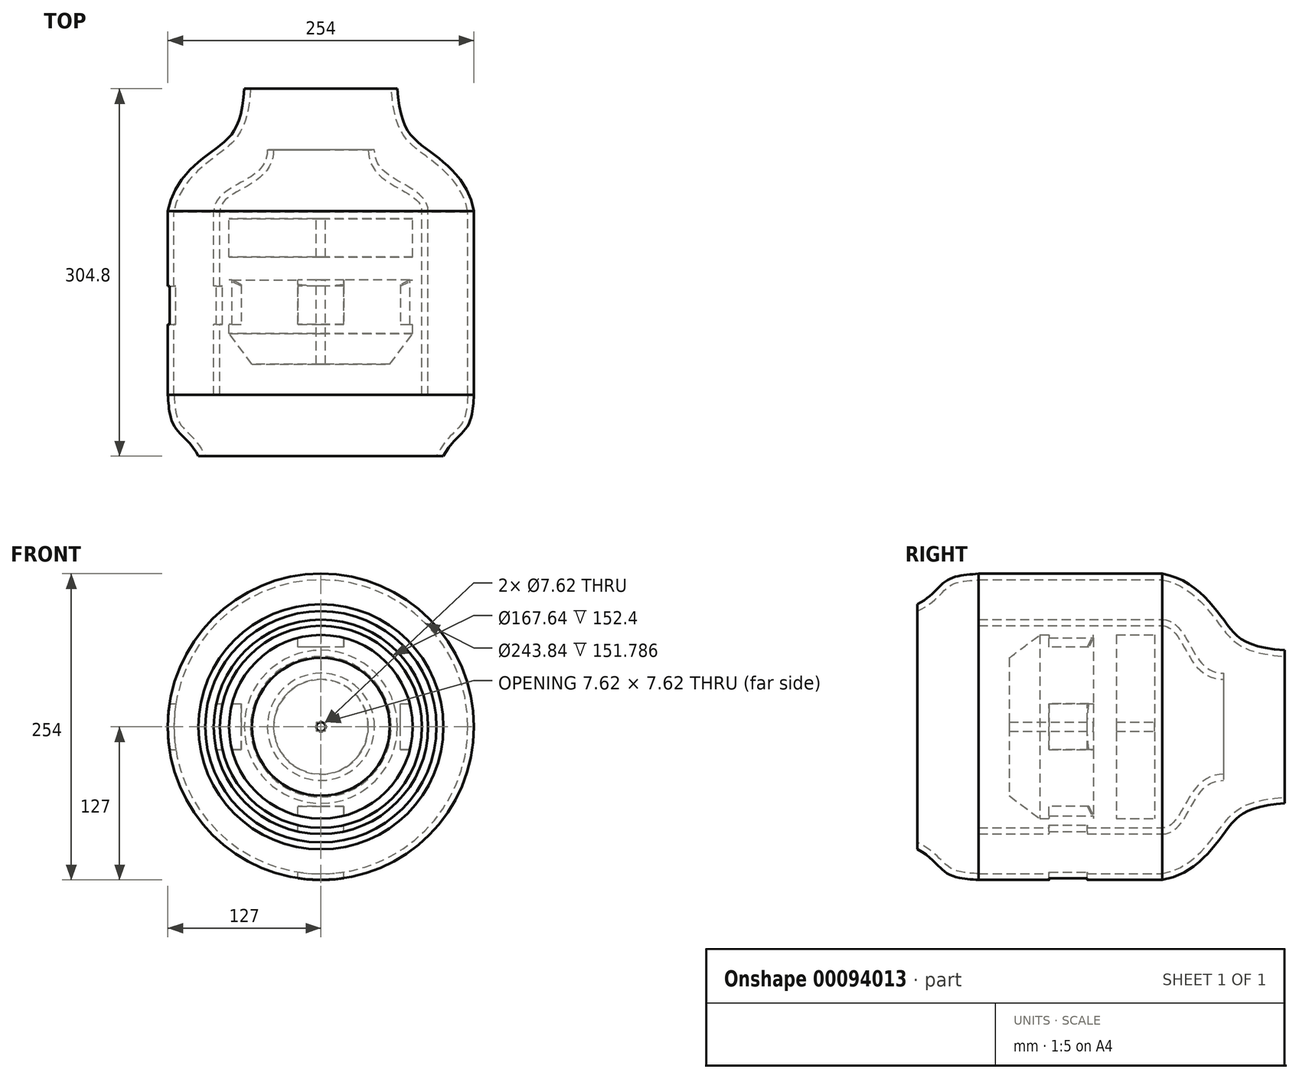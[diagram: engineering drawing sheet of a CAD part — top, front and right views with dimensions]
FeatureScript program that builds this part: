
annotation { "Feature Type Name" : "Feature", "Feature Type Description" : "" }
export const myFeature = defineFeature(function(context is Context, id is Id, definition is map)
    precondition{}
    {
        {
            var Q0;
            Q0=qCreatedBy(makeId("Right.planeOp"),FACE);
            var sketch = newSketch(context, id + "F0", { "sketchPlane" : qUnion([Q0])});
            skLineSegment(sketch, "E0", {"start": v(152.4, 0) * mm, "end": v(-152.4, 0) * mm});
            skPoint(sketch, "E1", {"position": v(0, 0) * mm});
            skLineSegment(sketch, "E2", {"start": v(-152.4, 0) * mm, "end": v(-152.4, 101.6) * mm});
            skLineSegment(sketch, "E3", {"start": v(-152.4, 101.6) * mm, "end": v(-127, 101.6) * mm, "construction": true});
            skLineSegment(sketch, "E4", {"start": v(-127, 101.6) * mm, "end": v(-127, 121.92) * mm, "construction": true});
            skLineSegment(sketch, "E5", {"start": v(-127, 101.6) * mm, "end": v(-101.6, 101.6) * mm, "construction": true});
            skLineSegment(sketch, "E6", {"start": v(-101.6, 101.6) * mm, "end": v(-101.6, 127) * mm, "construction": true});
            skFitSpline(sketch, "E7", {"points": [v(-152.4, 101.6) * mm, v(-127, 121.92) * mm, v(-101.6, 127) * mm], "startDerivative": vector(70.98, 35.75) * mm, "endDerivative": vector(55.23, 4.25) * mm});
            skLineSegment(sketch, "E8", {"start": v(-101.6, 127) * mm, "end": v(50.8, 127) * mm});
            skPoint(sketch, "E9", {"position": v(101.6, 0) * mm});
            skLineSegment(sketch, "E10", {"start": v(101.6, 0) * mm, "end": v(101.6, 88.9) * mm, "construction": true});
            skLineSegment(sketch, "E11", {"start": v(152.4, 0) * mm, "end": v(152.4, 63.5) * mm});
            skFitSpline(sketch, "E12", {"points": [v(50.8, 127) * mm, v(101.6, 88.9) * mm, v(152.4, 63.5) * mm], "startDerivative": vector(144.88, -23.56) * mm, "endDerivative": vector(213.2, -14.75) * mm});
            skLineSegment(sketch, "E13", {"start": v(-101.6, 127) * mm, "end": v(-101.6, 0) * mm, "construction": true});
            skLineSegment(sketch, "E14", {"start": v(-101.6, 0) * mm, "end": v(-101.6, 88.9) * mm});
            skLineSegment(sketch, "E15", {"start": v(-101.6, 88.9) * mm, "end": v(50.8, 88.9) * mm});
            skPoint(sketch, "E16", {"position": v(76.2, 0) * mm});
            skLineSegment(sketch, "E17", {"start": v(101.6, 0) * mm, "end": v(101.6, 44.45) * mm, "construction": true});
            skLineSegment(sketch, "E18", {"start": v(76.2, 0) * mm, "end": v(76.2, 63.5) * mm, "construction": true});
            skFitSpline(sketch, "E19", {"points": [v(50.8, 88.9) * mm, v(76.2, 63.5) * mm, v(101.6, 44.45) * mm], "startDerivative": vector(73.92, 0) * mm, "endDerivative": vector(78.63, 0) * mm});
            skLineSegment(sketch, "E20", {"start": v(101.6, 44.45) * mm, "end": v(76.2, 44.45) * mm, "construction": true});
            skLineSegment(sketch, "E21", {"start": v(50.8, 88.9) * mm, "end": v(76.2, 88.9) * mm, "construction": true});
            skLineSegment(sketch, "E22", {"start": v(101.6, 44.45) * mm, "end": v(101.6, 0) * mm});
            skPoint(sketch, "E23", {"position": v(-76.2, 0) * mm});
            skLineSegment(sketch, "E24", {"start": v(-76.2, 0) * mm, "end": v(-76.2, 57.15) * mm});
            skPoint(sketch, "E25", {"position": v(-50.8, 0) * mm});
            skLineSegment(sketch, "E26", {"start": v(-50.8, 0) * mm, "end": v(-50.8, 76.2) * mm, "construction": true});
            skLineSegment(sketch, "E27", {"start": v(-76.2, 57.15) * mm, "end": v(-50.8, 76.2) * mm});
            skLineSegment(sketch, "E28", {"start": v(-50.8, 76.2) * mm, "end": v(-6.35, 76.2) * mm});
            skLineSegment(sketch, "E29", {"start": v(-6.35, 76.2) * mm, "end": v(-6.35, 0) * mm});
            skLineSegment(sketch, "E30", {"start": v(-6.35, 0) * mm, "end": v(-76.2, 0) * mm});
            skPoint(sketch, "E31", {"position": v(12.7, 0) * mm});
            skLineSegment(sketch, "E32", {"start": v(12.7, 0) * mm, "end": v(12.7, 76.2) * mm});
            skLineSegment(sketch, "E33", {"start": v(12.7, 76.2) * mm, "end": v(44.45, 76.2) * mm});
            skLineSegment(sketch, "E34.bottom", {"start": v(-93.42, 127) * mm, "end": v(-7.63, 127) * mm});
            skLineSegment(sketch, "E35", {"start": v(44.45, 76.2) * mm, "end": v(44.45, 0) * mm});
            skSolve(sketch);
        }
        {
            var Q0;
            {var subQ4=sQuery(id+"F0.wireOp",EDGE,"E2");Q0=makeQuery(id+"F0.imprint","IMPRINT",FACE,{"disambiguationData":[TD([[makeQuery(id+"F0.imprint","IMPRINT",EDGE,{"derivedFrom":subQ4}),-1.0]])]});}
            var Q1;
            {var subQ0=sQuery(id+"F0.wireOp",EDGE,"E14");Q1=makeQuery(id+"F0.imprint","IMPRINT",FACE,{"disambiguationData":[TD([[makeQuery(id+"F0.imprint","IMPRINT",EDGE,{"derivedFrom":subQ0}),-1.0]])]});}
            var Q2;
            {var subQ0=sQuery(id+"F0.wireOp",EDGE,"E32");Q2=makeQuery(id+"F0.imprint","IMPRINT",FACE,{"disambiguationData":[TD([[makeQuery(id+"F0.imprint","IMPRINT",EDGE,{"derivedFrom":subQ0}),-1.0]])]});}
            var Q3;
            Q3=makeQuery(id+"F0.imprint","IMPRINT",FACE,{"disambiguationData":[TD([[makeQuery(id+"F0.imprint","IMPRINT",EDGE,{"derivedFrom":sQuery(id+"F0.wireOp",EDGE,"E24")}),-1.0]])]});
            var Q4;
            Q4=sQuery(id+"F0.wireOp",EDGE,"E0");
            revolve(context, id + "F1", {"entities" : qUnion([Q0, Q1, Q2, Q3]), "axis" : qUnion([Q4]), "revolveType" : RevolveType.FULL});
        }
        {
            var Q0;
            Q0=makeQuery(id+"F1.opRevolve","SWEPT_FACE",FACE,{"disambiguationData":[OSD([sQuery(id+"F0.wireOp",EDGE,"E2")])]});
            var Q1;
            Q1=makeQuery(id+"F1.opRevolve","SWEPT_FACE",FACE,{"disambiguationData":[OSD([sQuery(id+"F0.wireOp",EDGE,"E11")])]});
            shell(context, id + "F2", {"entities" : qUnion([Q0, Q1]), "thickness" : 5.08 * mm});
        }
        {
            var Q0;
            Q0=qCreatedBy(makeId("Front.planeOp"),FACE);
            var sketch = newSketch(context, id + "F3", { "sketchPlane" : qUnion([Q0])});
            skCircle(sketch, "E36", {"center": v(0, 0) * mm, "radius": 3.18 * mm});
            skCircle(sketch, "E37", {"center": v(0, 0) * mm, "radius": 3.81 * mm});
            skSolve(sketch);
        }
        {
            var Q0;
            {var subQ0=sQuery(id+"F0.wireOp",EDGE,"E14");Q0=makeQuery(id+"F0.imprint","IMPRINT",FACE,{"disambiguationData":[TD([[makeQuery(id+"F0.imprint","IMPRINT",EDGE,{"derivedFrom":subQ0}),-1.0]])]});}
            var Q1;
            Q1=makeQuery(id+"F0.imprint","IMPRINT",FACE,{"disambiguationData":[TD([[makeQuery(id+"F0.imprint","IMPRINT",EDGE,{"derivedFrom":sQuery(id+"F0.wireOp",EDGE,"E24")}),-1.0]])]});
            var Q2;
            {var subQ0=sQuery(id+"F0.wireOp",EDGE,"E32");Q2=makeQuery(id+"F0.imprint","IMPRINT",FACE,{"disambiguationData":[TD([[makeQuery(id+"F0.imprint","IMPRINT",EDGE,{"derivedFrom":subQ0}),-1.0]])]});}
            var Q3;
            Q3=sQuery(id+"F0.wireOp",EDGE,"E0");
            revolve(context, id + "F4", {"entities" : qUnion([Q0, Q1, Q2]), "axis" : qUnion([Q3]), "revolveType" : RevolveType.FULL});
        }
        {
            var Q0;
            Q0=makeQuery(id+"F4.opRevolve","SWEPT_FACE",FACE,{"disambiguationData":[OSD([sQuery(id+"F0.wireOp",EDGE,"E14")])]});
            var Q1;
            Q1=makeQuery(id+"F4.opRevolve","SWEPT_FACE",FACE,{"disambiguationData":[OSD([sQuery(id+"F0.wireOp",EDGE,"E22")])]});
            shell(context, id + "F5", {"entities" : qUnion([Q0, Q1]), "thickness" : 5.08 * mm});
        }
        {
            var Q0;
            Q0=makeQuery(id+"F0.imprint","IMPRINT",FACE,{"disambiguationData":[TD([[makeQuery(id+"F0.imprint","IMPRINT",EDGE,{"derivedFrom":sQuery(id+"F0.wireOp",EDGE,"E24")}),-1.0]])]});
            var Q1;
            {var subQ0=sQuery(id+"F0.wireOp",EDGE,"E32");Q1=makeQuery(id+"F0.imprint","IMPRINT",FACE,{"disambiguationData":[TD([[makeQuery(id+"F0.imprint","IMPRINT",EDGE,{"derivedFrom":subQ0}),-1.0]])]});}
            var Q2;
            Q2=sQuery(id+"F0.wireOp",EDGE,"E0");
            revolve(context, id + "F6", {"entities" : qUnion([Q0, Q1]), "axis" : qUnion([Q2]), "revolveType" : RevolveType.FULL});
        }
        {
            var Q0;
            Q0=makeQuery(id+"F3.imprint","IMPRINT",FACE,{"disambiguationData":[TD([[makeQuery(id+"F3.imprint","IMPRINT",EDGE,{"derivedFrom":sQuery(id+"F3.wireOp",EDGE,"E36")}),-1.0]])]});
            var Q1;
            Q1=makeQuery(id+"F3.imprint","IMPRINT",FACE,{"disambiguationData":[TD([[makeQuery(id+"F3.imprint","IMPRINT",EDGE,{"derivedFrom":sQuery(id+"F3.wireOp",EDGE,"E36")}),1.0]])]});
            extrude(context, id + "F7", {"entities" : qUnion([Q0, Q1]), "operationType" : NewBodyOperationType.REMOVE, "endBound" : BoundingType.SYMMETRIC, "depth" : 2540 * mm});
        }
        {
            var Q0;
            Q0=qCreatedBy(makeId("Top.planeOp"),FACE);
            cPlane(context, id + "F8", {"entities" : qUnion([Q0]), "cplaneType" : CPlaneType.OFFSET, "offset" : 76.2 * mm, "width" : 152.4 * mm, "height" : 152.4 * mm});
        }
        {
            var Q0;
            Q0=qCreatedBy(id+"F8.planeOp",FACE);
            var sketch = newSketch(context, id + "F9", { "sketchPlane" : qUnion([Q0])});
            skPoint(sketch, "E38", {"position": v(0, -6.35) * mm});
            skLineSegment(sketch, "E39", {"start": v(0, -6.35) * mm, "end": v(19.05, -6.35) * mm, "construction": true});
            skLineSegment(sketch, "E40", {"start": v(19.05, -6.35) * mm, "end": v(19.05, -11.43) * mm, "construction": true});
            skLineSegment(sketch, "E41.bottom", {"start": v(19.05, -11.43) * mm, "end": v(-19.05, -11.43) * mm});
            skLineSegment(sketch, "E41.top", {"start": v(19.05, -43.18) * mm, "end": v(-19.05, -43.18) * mm});
            skLineSegment(sketch, "E41.left", {"start": v(19.05, -11.43) * mm, "end": v(19.05, -43.18) * mm});
            skLineSegment(sketch, "E41.right", {"start": v(-19.05, -11.43) * mm, "end": v(-19.05, -43.18) * mm});
            skSolve(sketch);
        }
        {
            var Q0;
            Q0=makeQuery(id+"F9.imprint","IMPRINT",FACE,{"disambiguationData":[TD([[makeQuery(id+"F9.imprint","IMPRINT",EDGE,{"derivedFrom":sQuery(id+"F9.wireOp",EDGE,"E41.bottom")}),1.0]])]});
            extrude(context, id + "F10", {"entities" : qUnion([Q0]), "operationType" : NewBodyOperationType.REMOVE, "oppositeDirection" : true, "depth" : 10.16 * mm});
        }
        {
            var Q0;
            Q0 = qSketchRegion(id + "F9", true);
            extrude(context, id + "F11", {"entities" : qUnion([Q0]), "operationType" : NewBodyOperationType.REMOVE, "endBound" : BoundingType.THROUGH_ALL, "oppositeDirection" : true, "depth" : 25.4 * mm, "hasSecondDirection" : true, "secondDirectionOppositeDirection" : true, "secondDirectionDepth" : 142.24 * mm});
        }
        {
            var Q0;
            Q0=qCreatedBy(makeId("Right.planeOp"),FACE);
            cPlane(context, id + "F12", {"entities" : qUnion([Q0]), "cplaneType" : CPlaneType.OFFSET, "offset" : 76.2 * mm, "width" : 152.4 * mm, "height" : 152.4 * mm});
        }
        {
            var Q0;
            Q0=qCreatedBy(id+"F12.planeOp",FACE);
            var sketch = newSketch(context, id + "F13", { "sketchPlane" : qUnion([Q0])});
            skPoint(sketch, "E42", {"position": v(-6.35, 0) * mm});
            skLineSegment(sketch, "E43", {"start": v(-6.35, 0) * mm, "end": v(-11.43, 0) * mm, "construction": true});
            skLineSegment(sketch, "E44", {"start": v(-11.43, 0) * mm, "end": v(-27.3, 0) * mm, "construction": true});
            skLineSegment(sketch, "E45.bottom", {"start": v(-11.43, -19.05) * mm, "end": v(-43.18, -19.05) * mm});
            skLineSegment(sketch, "E45.top", {"start": v(-11.43, 19.05) * mm, "end": v(-43.18, 19.05) * mm});
            skLineSegment(sketch, "E45.left", {"start": v(-11.43, -19.05) * mm, "end": v(-11.43, 19.05) * mm});
            skLineSegment(sketch, "E45.right", {"start": v(-43.18, -19.05) * mm, "end": v(-43.18, 19.05) * mm});
            skPoint(sketch, "E45.middle", {"position": v(-27.3, 0) * mm});
            skSolve(sketch);
        }
        {
            var Q0;
            Q0=makeQuery(id+"F13.imprint","IMPRINT",FACE,{"disambiguationData":[TD([[makeQuery(id+"F13.imprint","IMPRINT",EDGE,{"derivedFrom":sQuery(id+"F13.wireOp",EDGE,"E45.bottom")}),-1.0]])]});
            extrude(context, id + "F14", {"entities" : qUnion([Q0]), "operationType" : NewBodyOperationType.REMOVE, "oppositeDirection" : true, "depth" : 10.16 * mm});
        }
        {
            var Q0;
            Q0 = qSketchRegion(id + "F13", true);
            var Q1;
            Q1 = qConstructionFilter(qBodyType(qCreatedBy(id + "F13" ,EDGE), BodyType.WIRE), ConstructionObject.NO);
            extrude(context, id + "F15", {"entities" : qUnion([Q0]), "operationType" : NewBodyOperationType.REMOVE, "surfaceEntities" : qUnion([Q1]), "endBound" : BoundingType.THROUGH_ALL, "oppositeDirection" : true, "depth" : 25.4 * mm, "hasSecondDirection" : true, "secondDirectionOppositeDirection" : true, "secondDirectionDepth" : 142.24 * mm});
        }
        {
            var Q0;
            Q0=makeQuery(id+"F10.boolean.opBoolean","INTERSECT",EDGE,{"derivedFrom":[makeQuery(id+"F6.opRevolve","SWEPT_FACE",FACE,{"disambiguationData":[OSD([sQuery(id+"F0.wireOp",EDGE,"E28")])]}),makeQuery(id+"F10.opExtrude","SWEPT_FACE",FACE,{"disambiguationData":[OSD([sQuery(id+"F9.wireOp",EDGE,"E41.bottom")])]})]});
            var Q1;
            Q1=makeQuery(id+"F11.boolean.opBoolean","INTERSECT",EDGE,{"derivedFrom":[makeQuery(id+"F6.opRevolve","SWEPT_FACE",FACE,{"disambiguationData":[OSD([sQuery(id+"F0.wireOp",EDGE,"E28")])]}),makeQuery(id+"F11.opExtrude","SWEPT_FACE",FACE,{"disambiguationData":[OSD([sQuery(id+"F9.wireOp",EDGE,"E41.bottom")])]})]});
            var Q2;
            Q2=makeQuery(id+"F15.boolean.opBoolean","INTERSECT",EDGE,{"derivedFrom":[makeQuery(id+"F6.opRevolve","SWEPT_FACE",FACE,{"disambiguationData":[OSD([sQuery(id+"F0.wireOp",EDGE,"E28")])]}),makeQuery(id+"F15.opExtrude","SWEPT_FACE",FACE,{"disambiguationData":[OSD([sQuery(id+"F13.wireOp",EDGE,"E45.left")])]})]});
            var Q3;
            Q3=makeQuery(id+"F14.boolean.opBoolean","INTERSECT",EDGE,{"derivedFrom":[makeQuery(id+"F6.opRevolve","SWEPT_FACE",FACE,{"disambiguationData":[OSD([sQuery(id+"F0.wireOp",EDGE,"E28")])]}),makeQuery(id+"F14.opExtrude","SWEPT_FACE",FACE,{"disambiguationData":[OSD([sQuery(id+"F13.wireOp",EDGE,"E45.left")])]})]});
            chamfer(context, id + "F16", {"entities" : qUnion([Q0, Q1, Q2, Q3]), "chamferType" : ChamferType.TWO_OFFSETS, "width1" : 5.08 * mm, "oppositeDirection" : false, "width2" : 10.16 * mm, "tangentPropagation" : true});
        }
    });
